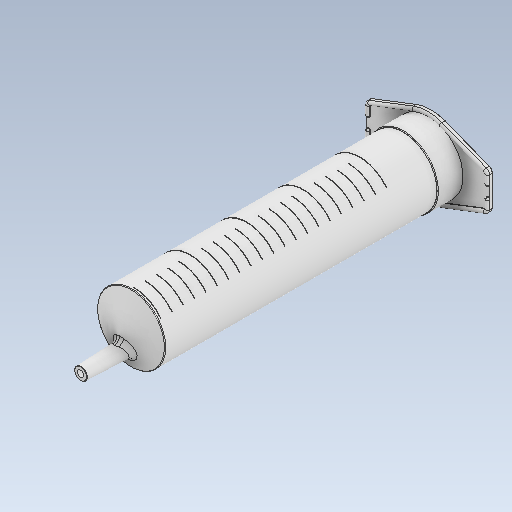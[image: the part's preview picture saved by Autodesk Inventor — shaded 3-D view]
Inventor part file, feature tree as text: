
AUTODESK INVENTOR PART (.ipt)
format: ipt  version: 2020 (Build 240168000, 168)  size: 849,408 bytes
history: native  units: in
note: dims shown in document units (in); Inventor stores cm internally (conversion verified against a paired STEP export)
features: fillet x1
ambient origin geometry x8: Origin, YZ Plane, XZ Plane, XY Plane, X Axis, Y Axis, Z Axis, Center Point
bodies: Solid1 (feature_tree)
feature tree (1):
  fillet  "Fillet8"  [1 undecoded]
note: 1 required parameter value undecoded (feature->parameter linkage not recoverable at this tier; creation-order binding heuristic only, values carry confidence <= 0.55)
